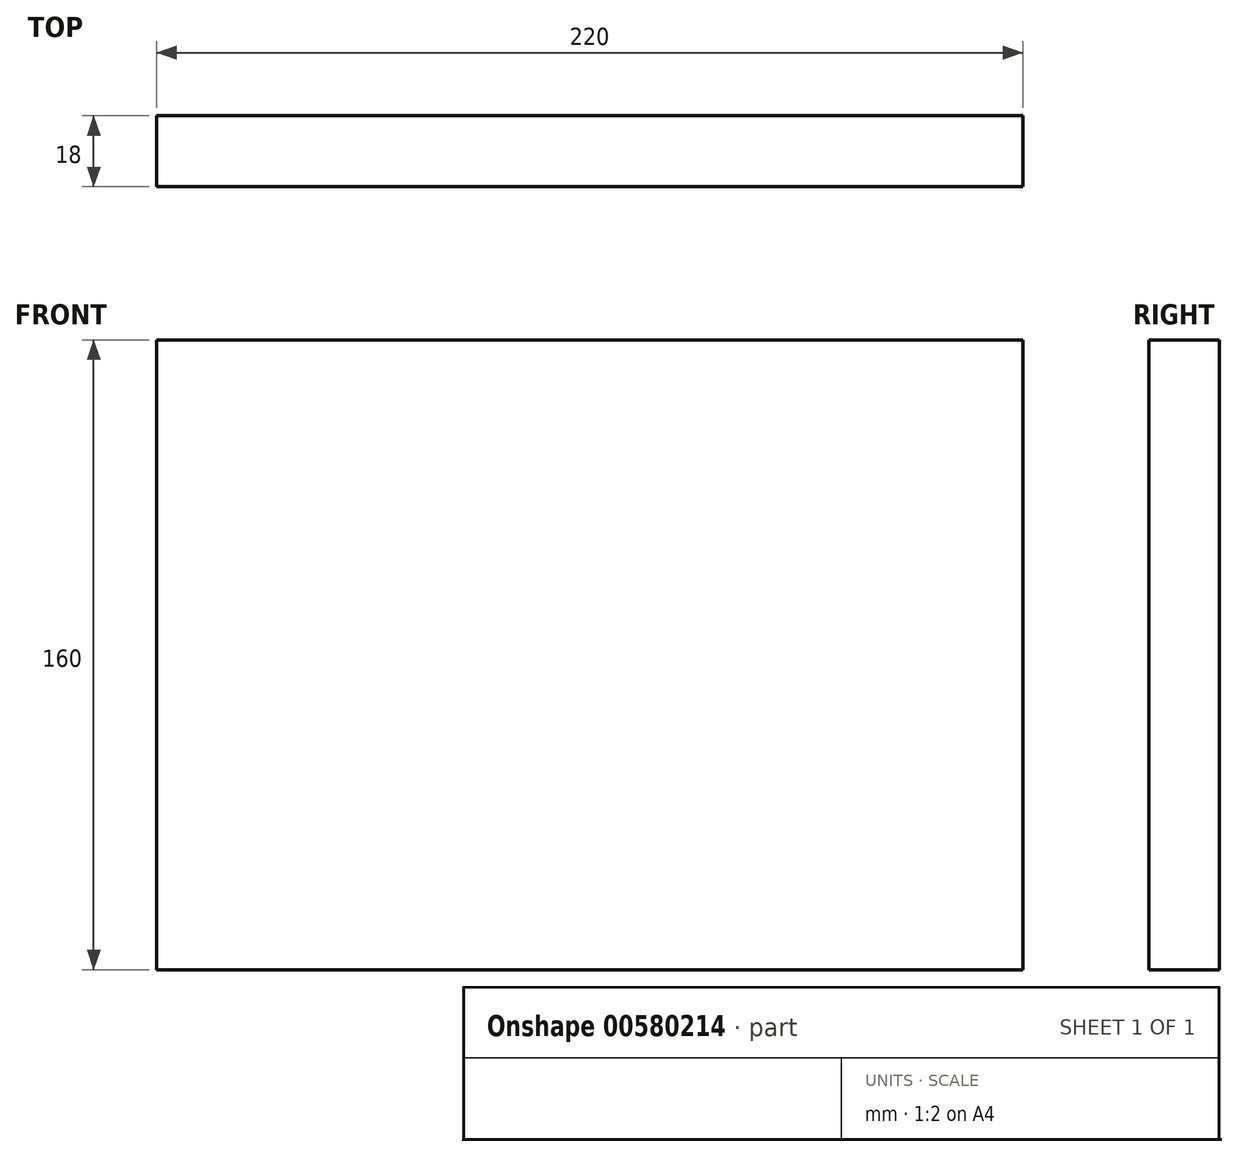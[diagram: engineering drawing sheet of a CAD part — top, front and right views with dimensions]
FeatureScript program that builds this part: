
annotation { "Feature Type Name" : "Feature", "Feature Type Description" : "" }
export const myFeature = defineFeature(function(context is Context, id is Id, definition is map)
    precondition{}
    {
        {
            var Q0;
            Q0=qCreatedBy(makeId("Front.planeOp"),FACE);
            var sketch = newSketch(context, id + "F0", { "sketchPlane" : qUnion([Q0])});
            skLineSegment(sketch, "E0.bottom", {"start": v(110, 80) * mm, "end": v(-110, 80) * mm});
            skLineSegment(sketch, "E0.top", {"start": v(110, -80) * mm, "end": v(-110, -80) * mm});
            skLineSegment(sketch, "E0.left", {"start": v(110, 80) * mm, "end": v(110, -80) * mm});
            skLineSegment(sketch, "E0.right", {"start": v(-110, 80) * mm, "end": v(-110, -80) * mm});
            skPoint(sketch, "E0.middle", {"position": v(0, 0) * mm});
            skSolve(sketch);
        }
        {
            var Q0;
            Q0=makeQuery(id+"F0.imprint","IMPRINT",FACE,{"disambiguationData":[TD([[makeQuery(id+"F0.imprint","IMPRINT",EDGE,{"derivedFrom":sQuery(id+"F0.wireOp",EDGE,"E0.bottom")}),1.0]])]});
            extrude(context, id + "F1", {"entities" : qUnion([Q0]), "oppositeDirection" : true, "depth" : 18 * mm, "offsetDistance" : 25 * mm});
        }
    });
